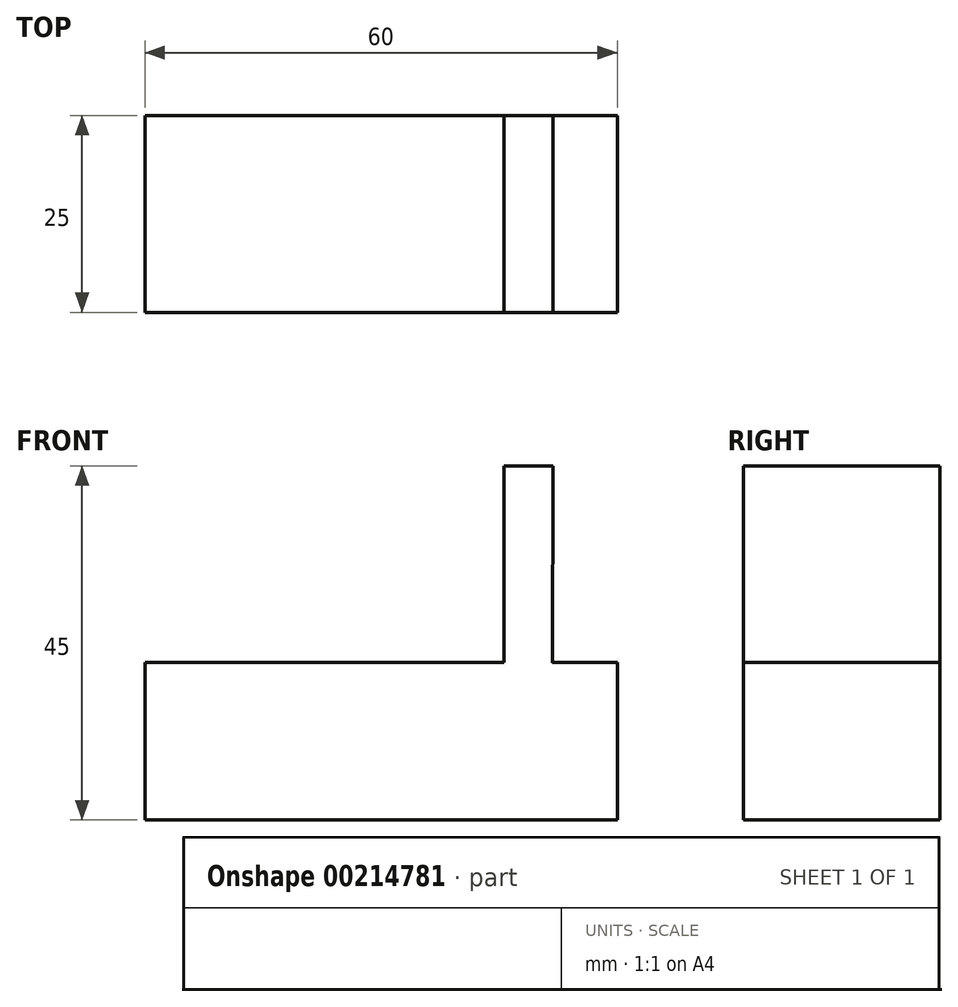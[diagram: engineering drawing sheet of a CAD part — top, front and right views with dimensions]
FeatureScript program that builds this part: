
annotation { "Feature Type Name" : "Feature", "Feature Type Description" : "" }
export const myFeature = defineFeature(function(context is Context, id is Id, definition is map)
    precondition{}
    {
        {
            var Q0;
            Q0=qCreatedBy(makeId("Front.planeOp"),FACE);
            var sketch = newSketch(context, id + "F0", { "sketchPlane" : qUnion([Q0])});
            skLineSegment(sketch, "E0.bottom", {"start": v(-67.64, 9.66) * mm, "end": v(-7.64, 9.66) * mm});
            skLineSegment(sketch, "E0.top", {"start": v(-67.64, -10.34) * mm, "end": v(-7.64, -10.34) * mm});
            skLineSegment(sketch, "E0.left", {"start": v(-67.64, 9.66) * mm, "end": v(-67.64, -10.34) * mm});
            skLineSegment(sketch, "E0.right", {"start": v(-7.64, 9.66) * mm, "end": v(-7.64, -10.34) * mm});
            skFitSpline(sketch, "E1", {"points": [v(-22.06, 9.66) * mm, v(7.49, 35.05) * mm, v(25.8, 16.25) * mm, v(42.65, 31.15) * mm, v(58.52, 36.03) * mm], "startDerivative": vector(102.2, 139.9) * mm, "endDerivative": vector(80.01, 3.52) * mm});
            skFitSpline(sketch, "E2.0", {"points": [v(-18.02, 6.7) * mm, v(-16.96, 8.16) * mm, v(-14.84, 11.07) * mm, v(-11.7, 15.26) * mm, v(-8.63, 19.2) * mm, v(-5.66, 22.73) * mm, v(-2.81, 25.76) * mm, v(-0.17, 28.14) * mm, v(1.76, 29.47) * mm, v(3.05, 30.13) * mm, v(3.86, 30.43) * mm, v(4.5, 30.56) * mm, v(4.87, 30.58) * mm, v(5.13, 30.55) * mm, v(5.3, 30.52) * mm, v(5.49, 30.47) * mm, v(5.68, 30.4) * mm, v(5.93, 30.26) * mm, v(6.35, 30.01) * mm, v(6.99, 29.53) * mm, v(7.88, 28.7) * mm, v(9.17, 27.29) * mm, v(10.91, 25.06) * mm, v(12.72, 22.5) * mm, v(14.2, 20.41) * mm, v(15.35, 18.85) * mm, v(16.53, 17.32) * mm, v(17.78, 15.85) * mm, v(19.13, 14.46) * mm, v(20.4, 13.4) * mm, v(21.56, 12.62) * mm, v(22.52, 12.1) * mm, v(23.4, 11.73) * mm, v(24.17, 11.5) * mm, v(24.77, 11.35) * mm, v(25.39, 11.25) * mm, v(26.21, 11.17) * mm, v(27.23, 11.18) * mm, v(28.39, 11.35) * mm, v(29.83, 11.74) * mm, v(31.42, 12.46) * mm, v(33.05, 13.52) * mm, v(34.5, 14.7) * mm, v(35.84, 15.98) * mm, v(37.1, 17.33) * mm, v(38.72, 19.18) * mm, v(40.26, 21.07) * mm, v(41.75, 22.89) * mm, v(42.84, 24.19) * mm, v(43.9, 25.38) * mm, v(44.75, 26.27) * mm, v(45.4, 26.9) * mm, v(45.85, 27.3) * mm, v(46.3, 27.68) * mm, v(46.88, 28.14) * mm, v(47.6, 28.63) * mm, v(48.76, 29.3) * mm, v(50.21, 29.92) * mm, v(52.06, 30.42) * mm, v(54.09, 30.74) * mm, v(56.3, 30.93) * mm, v(57.9, 31) * mm, v(58.74, 31.03) * mm]});
            skArc(sketch, "E3", {"start": v(58.52, 36.03) * mm, "mid": v(61.13, 33.64) * mm, "end": v(58.74, 31.03) * mm});
            skLineSegment(sketch, "E4", {"start": v(-22.06, 9.66) * mm, "end": v(-15.87, 9.65) * mm});
            skSolve(sketch);
        }
        {
            var Q0;
            Q0=makeQuery(id+"F0.imprint","IMPRINT",FACE,{"disambiguationData":[TD([[makeQuery(id+"F0.imprint","IMPRINT",EDGE,{"derivedFrom":sQuery(id+"F0.wireOp",EDGE,"E0.top")}),1.0]])]});
            extrude(context, id + "F1", {"entities" : qUnion([Q0]), "depth" : 25 * mm});
        }
        {
            var Q0;
            Q0=makeQuery(id+"F1.opExtrude","SWEPT_FACE",FACE,{"disambiguationData":[OSD([sQuery(id+"F0.wireOp",EDGE,"E4")])]});
            extrude(context, id + "F2", {"entities" : qUnion([Q0]), "operationType" : NewBodyOperationType.ADD, "depth" : 25 * mm});
        }
    });
